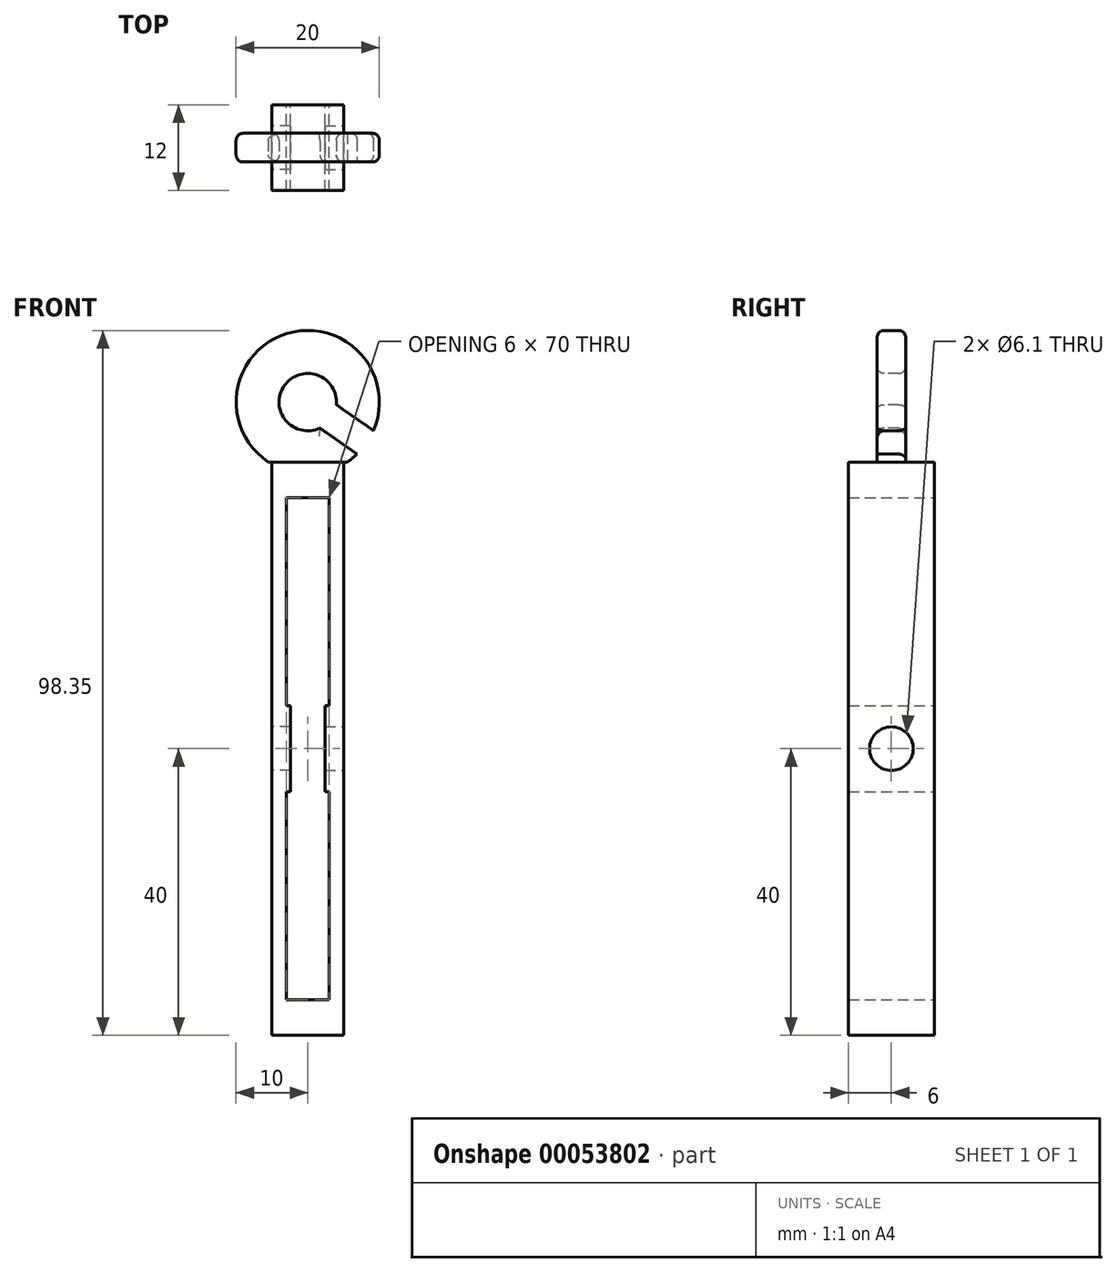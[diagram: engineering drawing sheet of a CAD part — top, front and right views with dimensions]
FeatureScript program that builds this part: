
annotation { "Feature Type Name" : "Feature", "Feature Type Description" : "" }
export const myFeature = defineFeature(function(context is Context, id is Id, definition is map)
    precondition{}
    {
        {
            var Q0;
            Q0=qCreatedBy(makeId("Right.planeOp"),FACE);
            var sketch = newSketch(context, id + "F0", { "sketchPlane" : qUnion([Q0])});
            skCircle(sketch, "E0", {"center": v(0, 0) * mm, "radius": 3.05 * mm});
            skLineSegment(sketch, "E1", {"start": v(-13.5, 0) * mm, "end": v(18.06, 0) * mm, "construction": true});
            skLineSegment(sketch, "E2", {"start": v(0, 10.88) * mm, "end": v(0, -11.26) * mm, "construction": true});
            skLineSegment(sketch, "E3.bottom", {"start": v(-6, 40) * mm, "end": v(6, 40) * mm});
            skLineSegment(sketch, "E3.top", {"start": v(-6, -40) * mm, "end": v(6, -40) * mm});
            skLineSegment(sketch, "E3.left", {"start": v(-6, 40) * mm, "end": v(-6, -40) * mm});
            skLineSegment(sketch, "E3.right", {"start": v(6, 40) * mm, "end": v(6, -40) * mm});
            skLineSegment(sketch, "E4", {"start": v(0, 40) * mm, "end": v(0, -40) * mm, "construction": true});
            skCircle(sketch, "E5", {"center": v(0, 0) * mm, "radius": 6 * mm});
            skSolve(sketch);
        }
        {
            var Q0;
            {var subQ0=sQuery(id+"F0.wireOp",EDGE,"E3.bottom");Q0=makeQuery(id+"F0.imprint","IMPRINT",FACE,{"disambiguationData":[TD([[makeQuery(id+"F0.imprint","IMPRINT",EDGE,{"derivedFrom":subQ0}),-1.0]])]});}
            var Q1;
            Q1=makeQuery(id+"F0.imprint","IMPRINT",FACE,{"disambiguationData":[TD([[makeQuery(id+"F0.imprint","IMPRINT",EDGE,{"derivedFrom":sQuery(id+"F0.wireOp",EDGE,"E0")}),-1.0]])]});
            var Q2;
            {var subQ0=sQuery(id+"F0.wireOp",EDGE,"E3.top");Q2=makeQuery(id+"F0.imprint","IMPRINT",FACE,{"disambiguationData":[TD([[makeQuery(id+"F0.imprint","IMPRINT",EDGE,{"derivedFrom":subQ0}),1.0]])]});}
            extrude(context, id + "F1", {"entities" : qUnion([Q0, Q1, Q2]), "depth" : 2 * mm});
        }
        {
            var Q0;
            Q0=makeQuery(id+"F1.opExtrude","CAP_FACE",FACE,{"disambiguationData":[OSD([sQuery(id+"F0.wireOp",EDGE,"E0"),sQuery(id+"F0.wireOp",EDGE,"E3.bottom"),sQuery(id+"F0.wireOp",EDGE,"E3.top"),sQuery(id+"F0.wireOp",EDGE,"E3.left"),sQuery(id+"F0.wireOp",EDGE,"E3.right")])],"isStart":false});
            var sketch = newSketch(context, id + "F2", { "sketchPlane" : qUnion([Q0])});
            skLineSegment(sketch, "E6.bottom", {"start": v(-6, 40) * mm, "end": v(6, 40) * mm});
            skLineSegment(sketch, "E6.top", {"start": v(-6, 35) * mm, "end": v(6, 35) * mm});
            skLineSegment(sketch, "E6.left", {"start": v(-6, 40) * mm, "end": v(-6, 35) * mm});
            skLineSegment(sketch, "E6.right", {"start": v(6, 40) * mm, "end": v(6, 35) * mm});
            skLineSegment(sketch, "E7.bottom", {"start": v(-6, -35) * mm, "end": v(6, -35) * mm});
            skLineSegment(sketch, "E7.top", {"start": v(-6, -40) * mm, "end": v(6, -40) * mm});
            skLineSegment(sketch, "E7.left", {"start": v(-6, -35) * mm, "end": v(-6, -40) * mm});
            skLineSegment(sketch, "E7.right", {"start": v(6, -35) * mm, "end": v(6, -40) * mm});
            skLineSegment(sketch, "E8.bottom", {"start": v(-6, 6) * mm, "end": v(6, 6) * mm});
            skLineSegment(sketch, "E8.top", {"start": v(-6, -6) * mm, "end": v(6, -6) * mm});
            skLineSegment(sketch, "E8.left", {"start": v(-6, 6) * mm, "end": v(-6, -6) * mm});
            skLineSegment(sketch, "E8.right", {"start": v(6, 6) * mm, "end": v(6, -6) * mm});
            skSolve(sketch);
        }
        {
            var Q0;
            Q0=makeQuery(id+"F2.imprint","IMPRINT",FACE,{"disambiguationData":[TD([[makeQuery(id+"F2.imprint","IMPRINT",EDGE,{"derivedFrom":sQuery(id+"F2.wireOp",EDGE,"E6.bottom")}),-1.0]])]});
            var Q1;
            Q1=makeQuery(id+"F2.imprint","IMPRINT",FACE,{"disambiguationData":[TD([[makeQuery(id+"F2.imprint","IMPRINT",EDGE,{"derivedFrom":sQuery(id+"F2.wireOp",EDGE,"E7.bottom")}),-1.0]])]});
            extrude(context, id + "F3", {"entities" : qUnion([Q0, Q1]), "operationType" : NewBodyOperationType.ADD, "depth" : 3 * mm});
        }
        {
            var Q0;
            Q0=makeQuery(id+"F2.imprint","IMPRINT",FACE,{"disambiguationData":[TD([[makeQuery(id+"F2.imprint","IMPRINT",EDGE,{"derivedFrom":sQuery(id+"F2.wireOp",EDGE,"E8.bottom")}),-1.0]])]});
            extrude(context, id + "F4", {"entities" : qUnion([Q0]), "operationType" : NewBodyOperationType.ADD, "depth" : 0.6 * mm});
        }
        {
            var Q0;
            Q0=makeQuery(id+"F1.opExtrude","SWEPT_BODY",BODY,{"disambiguationData":[OSD([sQuery(id+"F0.wireOp",EDGE,"E0"),sQuery(id+"F0.wireOp",EDGE,"E3.bottom"),sQuery(id+"F0.wireOp",EDGE,"E3.top"),sQuery(id+"F0.wireOp",EDGE,"E3.left"),sQuery(id+"F0.wireOp",EDGE,"E3.right")])]});
            var Q1;
            Q1=makeQuery(id+"F3.opExtrude","CAP_FACE",FACE,{"disambiguationData":[OSD([sQuery(id+"F2.wireOp",EDGE,"E6.bottom"),sQuery(id+"F2.wireOp",EDGE,"E6.top"),sQuery(id+"F2.wireOp",EDGE,"E6.left"),sQuery(id+"F2.wireOp",EDGE,"E6.right")])],"isStart":false});
            mirror(context, id + "F5", {"operationType" : NewBodyOperationType.ADD, "entities" : qUnion([Q0]), "mirrorPlane" : qUnion([Q1])});
        }
        {
            var Q0;
            {var subQ0=makeQuery(id+"F3.boolean.opBoolean","MERGE",FACE,{"derivedFrom":[makeQuery(id+"F1.opExtrude","SWEPT_FACE",FACE,{"disambiguationData":[OSD([sQuery(id+"F0.wireOp",EDGE,"E3.left")])]}),makeQuery(id+"F3.opExtrude","SWEPT_FACE",FACE,{"disambiguationData":[OSD([sQuery(id+"F2.wireOp",EDGE,"E6.left")])]}),makeQuery(id+"F3.opExtrude","SWEPT_FACE",FACE,{"disambiguationData":[OSD([sQuery(id+"F2.wireOp",EDGE,"E7.left")])]})]});Q0=makeQuery(id+"F5.boolean.opBoolean","MERGE",FACE,{"derivedFrom":[subQ0,makeQuery(id+"F5.opPattern","COPY",FACE,{"derivedFrom":subQ0,"instanceName":"1"})]});}
            var sketch = newSketch(context, id + "F6", { "sketchPlane" : qUnion([Q0])});
            skLineSegment(sketch, "E9", {"start": v(5, 40) * mm, "end": v(5, -40) * mm, "construction": true});
            skCircle(sketch, "E10", {"center": v(5, 48.35) * mm, "radius": 10 * mm});
            skCircle(sketch, "E11", {"center": v(5, 48.35) * mm, "radius": 4 * mm});
            skLineSegment(sketch, "E12", {"start": v(-0.5, 40) * mm, "end": v(10.5, 40) * mm});
            skPoint(sketch, "E13", {"position": v(5, 35) * mm});
            skSolve(sketch);
        }
        {
            var Q0;
            Q0=makeQuery(id+"F6.imprint","IMPRINT",FACE,{"disambiguationData":[TD([[makeQuery(id+"F6.imprint","IMPRINT",EDGE,{"derivedFrom":sQuery(id+"F6.wireOp",EDGE,"E11")}),-1.0]])]});
            extrude(context, id + "F7", {"entities" : qUnion([Q0]), "operationType" : NewBodyOperationType.ADD, "oppositeDirection" : true, "depth" : 8 * mm, "hasSecondDirection" : true, "secondDirectionOppositeDirection" : true, "secondDirectionDepth" : 4 * mm});
        }
        {
            var Q0;
            Q0=makeQuery(id+"F7.opExtrude","CAP_FACE",FACE,{"disambiguationData":[OSD([sQuery(id+"F6.wireOp",EDGE,"E10"),sQuery(id+"F6.wireOp",EDGE,"E11"),sQuery(id+"F6.wireOp",EDGE,"E12")])],"isStart":true});
            var sketch = newSketch(context, id + "F8", { "sketchPlane" : qUnion([Q0])});
            skLineSegment(sketch, "E14", {"start": v(5, 48.35) * mm, "end": v(25.42, 34.05) * mm, "construction": true});
            skLineSegment(sketch, "E15", {"start": v(26.57, 35.7) * mm, "end": v(24.27, 32.41) * mm});
            skPoint(sketch, "E16", {"position": v(25.42, 34.05) * mm});
            skLineSegment(sketch, "E17", {"start": v(6.15, 49.99) * mm, "end": v(3.85, 46.71) * mm});
            skPoint(sketch, "E18", {"position": v(5, 48.35) * mm});
            skLineSegment(sketch, "E19", {"start": v(-5.97, 48.35) * mm, "end": v(31.04, 48.35) * mm, "construction": true});
            skLineSegment(sketch, "E20", {"start": v(6.15, 49.99) * mm, "end": v(26.57, 35.7) * mm});
            skLineSegment(sketch, "E21", {"start": v(24.27, 32.41) * mm, "end": v(3.85, 46.71) * mm});
            skSolve(sketch);
        }
        {
            var Q0;
            {var subQ0=sQuery(id+"F8.wireOp",EDGE,"E20");var subQ1=makeQuery(id+"F7.opExtrude","CAP_EDGE",EDGE,{"disambiguationData":[OSD([sQuery(id+"F6.wireOp",EDGE,"E10")])],"isStart":true});var subQ2=makeQuery(id+"F8.imprint","INTERSECT",VERTEX,{"derivedFrom":[subQ1,subQ0]});Q0=makeQuery(id+"F8.imprint","IMPRINT",FACE,{"disambiguationData":[TD([[makeQuery(id+"F8.imprint","IMPRINT",EDGE,{"disambiguationData":[TD([[subQ2,1.0]])],"derivedFrom":subQ0}),-1.0]])]});}
            extrude(context, id + "F9", {"entities" : qUnion([Q0]), "operationType" : NewBodyOperationType.REMOVE, "oppositeDirection" : true, "depth" : 25 * mm});
        }
        {
            var Q0;
            Q0=makeQuery(id+"F7.opExtrude","CAP_EDGE",EDGE,{"disambiguationData":[OSD([sQuery(id+"F6.wireOp",EDGE,"E11")])],"isStart":false});
            var Q1;
            {var subQ3=sQuery(id+"F6.wireOp",EDGE,"E10");Q1=makeQuery(id+"F9.boolean.opBoolean","SPLIT",EDGE,{"disambiguationData":[TD([makeQuery(id+"F9.opExtrude","SWEPT_FACE",FACE,{"disambiguationData":[OSD([sQuery(id+"F8.wireOp",EDGE,"E20")])]})])],"derivedFrom":makeQuery(id+"F7.opExtrude","CAP_EDGE",EDGE,{"disambiguationData":[OSD([subQ3])],"isStart":false})});}
            var Q2;
            {var subQ3=sQuery(id+"F6.wireOp",EDGE,"E10");Q2=makeQuery(id+"F9.boolean.opBoolean","SPLIT",EDGE,{"disambiguationData":[TD([makeQuery(id+"F9.opExtrude","SWEPT_FACE",FACE,{"disambiguationData":[OSD([sQuery(id+"F8.wireOp",EDGE,"E20")])]})])],"derivedFrom":makeQuery(id+"F7.opExtrude","CAP_EDGE",EDGE,{"disambiguationData":[OSD([subQ3])],"isStart":true})});}
            var Q3;
            Q3=makeQuery(id+"F7.opExtrude","CAP_EDGE",EDGE,{"disambiguationData":[OSD([sQuery(id+"F6.wireOp",EDGE,"E11")])],"isStart":true});
            var Q4;
            Q4=makeQuery(id+"F9.boolean.opBoolean","COPY",EDGE,{"derivedFrom":makeQuery(id+"F9.opExtrude","SWEPT_EDGE",EDGE,{"disambiguationData":[OSD([sQuery(id+"F6.wireOp",EDGE,"E10"),sQuery(id+"F8.wireOp",EDGE,"E20")])]})});
            var Q5;
            Q5=makeQuery(id+"F9.boolean.opBoolean","COPY",EDGE,{"derivedFrom":makeQuery(id+"F9.opExtrude","CAP_EDGE",EDGE,{"disambiguationData":[OSD([sQuery(id+"F8.wireOp",EDGE,"E21")])],"isStart":true})});
            var Q6;
            Q6=makeQuery(id+"F9.boolean.opBoolean","INTERSECT",EDGE,{"derivedFrom":[makeQuery(id+"F7.opExtrude","CAP_FACE",FACE,{"disambiguationData":[OSD([sQuery(id+"F6.wireOp",EDGE,"E10"),sQuery(id+"F6.wireOp",EDGE,"E11"),sQuery(id+"F6.wireOp",EDGE,"E12")])],"isStart":false}),makeQuery(id+"F9.opExtrude","SWEPT_FACE",FACE,{"disambiguationData":[OSD([sQuery(id+"F8.wireOp",EDGE,"E21")])]})]});
            fillet(context, id + "F10", {"entities" : qUnion([Q0, Q1, Q2, Q3, Q4, Q5, Q6]), "radius" : 1 * mm, "tangentPropagation" : true, "allowEdgeOverflow" : false});
        }
    });
